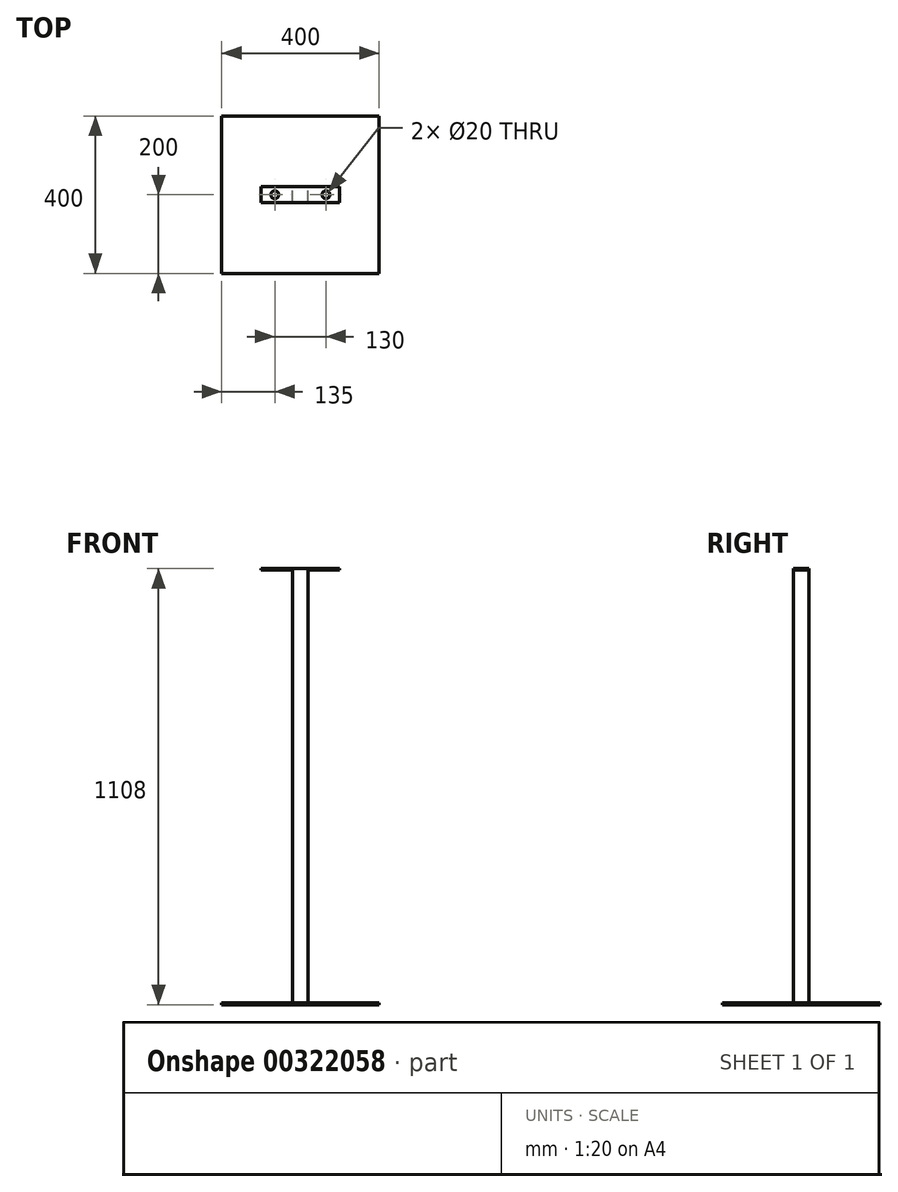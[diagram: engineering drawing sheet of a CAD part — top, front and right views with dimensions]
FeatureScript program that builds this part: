
annotation { "Feature Type Name" : "Feature", "Feature Type Description" : "" }
export const myFeature = defineFeature(function(context is Context, id is Id, definition is map)
    precondition{}
    {
        {
            var Q0;
            Q0=qCreatedBy(makeId("Top.planeOp"),FACE);
            var sketch = newSketch(context, id + "F0", { "sketchPlane" : qUnion([Q0])});
            skLineSegment(sketch, "E0.bottom", {"start": v(-200, -200) * mm, "end": v(200, -200) * mm});
            skLineSegment(sketch, "E0.top", {"start": v(-200, 200) * mm, "end": v(200, 200) * mm});
            skLineSegment(sketch, "E0.left", {"start": v(-200, -200) * mm, "end": v(-200, 200) * mm});
            skLineSegment(sketch, "E0.right", {"start": v(200, -200) * mm, "end": v(200, 200) * mm});
            skPoint(sketch, "E0.middle", {"position": v(0, 0) * mm});
            skSolve(sketch);
        }
        {
            var Q0;
            Q0=makeQuery(id+"F0.imprint","IMPRINT",FACE,{"disambiguationData":[TD([[makeQuery(id+"F0.imprint","IMPRINT",EDGE,{"derivedFrom":sQuery(id+"F0.wireOp",EDGE,"E0.bottom")}),1.0]])]});
            extrude(context, id + "F1", {"entities" : qUnion([Q0]), "depth" : 4 * mm});
        }
        {
            var Q0;
            Q0=makeQuery(id+"F1.opExtrude","CAP_FACE",FACE,{"disambiguationData":[OSD([sQuery(id+"F0.wireOp",EDGE,"E0.bottom"),sQuery(id+"F0.wireOp",EDGE,"E0.top"),sQuery(id+"F0.wireOp",EDGE,"E0.left"),sQuery(id+"F0.wireOp",EDGE,"E0.right")])],"isStart":false});
            var sketch = newSketch(context, id + "F2", { "sketchPlane" : qUnion([Q0])});
            skLineSegment(sketch, "E1.bottom", {"start": v(20, -20) * mm, "end": v(-20, -20) * mm});
            skLineSegment(sketch, "E1.top", {"start": v(20, 20) * mm, "end": v(-20, 20) * mm});
            skLineSegment(sketch, "E1.left", {"start": v(20, -20) * mm, "end": v(20, 20) * mm});
            skLineSegment(sketch, "E1.right", {"start": v(-20, -20) * mm, "end": v(-20, 20) * mm});
            skPoint(sketch, "E1.middle", {"position": v(0, 0) * mm});
            skSolve(sketch);
        }
        {
            var Q0;
            Q0=makeQuery(id+"F2.imprint","IMPRINT",FACE,{"disambiguationData":[TD([[makeQuery(id+"F2.imprint","IMPRINT",EDGE,{"derivedFrom":sQuery(id+"F2.wireOp",EDGE,"E1.bottom")}),-1.0]])]});
            extrude(context, id + "F3", {"entities" : qUnion([Q0]), "operationType" : NewBodyOperationType.ADD, "depth" : 1100 * mm});
        }
        {
            var Q0;
            Q0=makeQuery(id+"F3.opExtrude","CAP_FACE",FACE,{"disambiguationData":[OSD([sQuery(id+"F2.wireOp",EDGE,"E1.bottom"),sQuery(id+"F2.wireOp",EDGE,"E1.top"),sQuery(id+"F2.wireOp",EDGE,"E1.left"),sQuery(id+"F2.wireOp",EDGE,"E1.right")])],"isStart":false});
            var sketch = newSketch(context, id + "F4", { "sketchPlane" : qUnion([Q0])});
            skLineSegment(sketch, "E2.bottom", {"start": v(100, 20) * mm, "end": v(-100, 20) * mm});
            skLineSegment(sketch, "E2.top", {"start": v(100, -20) * mm, "end": v(-100, -20) * mm});
            skLineSegment(sketch, "E2.left", {"start": v(100, 20) * mm, "end": v(100, -20) * mm});
            skLineSegment(sketch, "E2.right", {"start": v(-100, 20) * mm, "end": v(-100, -20) * mm});
            skPoint(sketch, "E2.middle", {"position": v(0, 0) * mm});
            skSolve(sketch);
        }
        {
            var Q0;
            Q0 = qSketchRegion(id + "F4", true);
            extrude(context, id + "F5", {"entities" : qUnion([Q0]), "operationType" : NewBodyOperationType.ADD, "depth" : 4 * mm});
        }
        {
            var Q0;
            Q0=makeQuery(id+"F5.opExtrude","CAP_FACE",FACE,{"disambiguationData":[OSD([sQuery(id+"F4.wireOp",EDGE,"E2.bottom"),sQuery(id+"F4.wireOp",EDGE,"E2.top"),sQuery(id+"F4.wireOp",EDGE,"E2.left"),sQuery(id+"F4.wireOp",EDGE,"E2.right")])],"isStart":false});
            var sketch = newSketch(context, id + "F6", { "sketchPlane" : qUnion([Q0])});
            skCircle(sketch, "E3", {"center": v(-65, 0) * mm, "radius": 10 * mm});
            skSolve(sketch);
        }
        {
            var Q0;
            Q0=makeQuery(id+"F6.imprint","IMPRINT",FACE,{"disambiguationData":[TD([[makeQuery(id+"F6.imprint","IMPRINT",EDGE,{"derivedFrom":sQuery(id+"F6.wireOp",EDGE,"E3")}),-1.0]])]});
            var sketch = newSketch(context, id + "F7", { "sketchPlane" : qUnion([Q0])});
            skCircle(sketch, "E4", {"center": v(65, 0) * mm, "radius": 10 * mm});
            skSolve(sketch);
        }
        {
            var Q0;
            Q0=sQuery(id+"F6.wireOp",VERTEX,"E3.center");
            var Q1;
            Q1=makeQuery(id+"F1.opExtrude","SWEPT_BODY",BODY,{"disambiguationData":[OSD([sQuery(id+"F0.wireOp",EDGE,"E0.bottom"),sQuery(id+"F0.wireOp",EDGE,"E0.top"),sQuery(id+"F0.wireOp",EDGE,"E0.left"),sQuery(id+"F0.wireOp",EDGE,"E0.right")])]});
            hole(context, id + "F8", {"style" : HoleStyle.SIMPLE, "endStyle" : HoleEndStyle.BLIND, "holeDiameter" : 20 * mm, "holeDepth" : 20 * mm, "tappedDepth" : 12 * mm, "tapClearance" : 3, "startFromSketch" : true, "locations" : qUnion([Q0]), "scope" : qUnion([Q1])});
        }
        {
            var Q0;
            Q0=sQuery(id+"F7.wireOp",VERTEX,"E4.center");
            var Q1;
            Q1=makeQuery(id+"F1.opExtrude","SWEPT_BODY",BODY,{"disambiguationData":[OSD([sQuery(id+"F0.wireOp",EDGE,"E0.bottom"),sQuery(id+"F0.wireOp",EDGE,"E0.top"),sQuery(id+"F0.wireOp",EDGE,"E0.left"),sQuery(id+"F0.wireOp",EDGE,"E0.right")])]});
            hole(context, id + "F9", {"style" : HoleStyle.SIMPLE, "endStyle" : HoleEndStyle.BLIND, "holeDiameter" : 20 * mm, "holeDepth" : 20 * mm, "tappedDepth" : 12 * mm, "tapClearance" : 3, "startFromSketch" : true, "locations" : qUnion([Q0]), "scope" : qUnion([Q1])});
        }
    });
